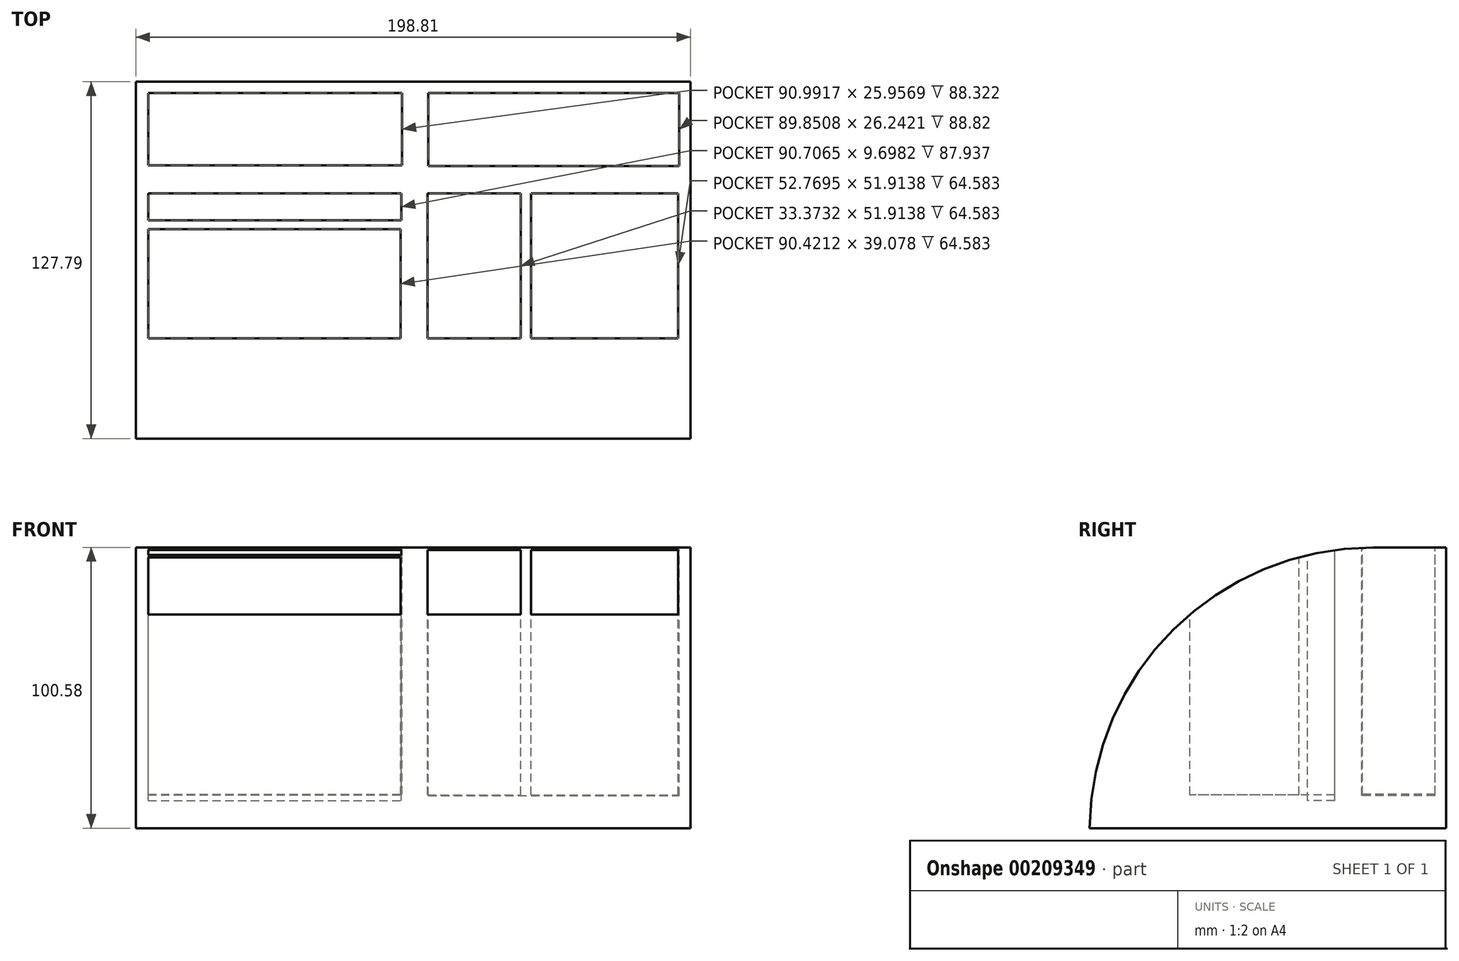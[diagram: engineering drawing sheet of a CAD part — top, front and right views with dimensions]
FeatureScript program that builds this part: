
annotation { "Feature Type Name" : "Feature", "Feature Type Description" : "" }
export const myFeature = defineFeature(function(context is Context, id is Id, definition is map)
    precondition{}
    {
        {
            var Q0;
            Q0=qCreatedBy(makeId("Top.planeOp"),FACE);
            var sketch = newSketch(context, id + "F0", { "sketchPlane" : qUnion([Q0])});
            skLineSegment(sketch, "E0.bottom", {"start": v(-100.12, 58.33) * mm, "end": v(98.7, 58.33) * mm});
            skLineSegment(sketch, "E0.top", {"start": v(-100.12, -69.46) * mm, "end": v(98.7, -69.46) * mm});
            skLineSegment(sketch, "E0.left", {"start": v(-100.12, 58.33) * mm, "end": v(-100.12, -69.46) * mm});
            skLineSegment(sketch, "E0.right", {"start": v(98.7, 58.33) * mm, "end": v(98.7, -69.46) * mm});
            skSolve(sketch);
        }
        {
            var Q0;
            Q0=makeQuery(id+"F0.imprint","IMPRINT",FACE,{"disambiguationData":[TD([[makeQuery(id+"F0.imprint","IMPRINT",EDGE,{"derivedFrom":sQuery(id+"F0.wireOp",EDGE,"E0.bottom")}),-1.0]])]});
            extrude(context, id + "F1", {"entities" : qUnion([Q0]), "oppositeDirection" : true, "depth" : 100.58 * mm});
        }
        {
            var Q0;
            Q0=makeQuery(id+"F1.opExtrude","CAP_EDGE",EDGE,{"disambiguationData":[OSD([sQuery(id+"F0.wireOp",EDGE,"E0.top")])],"isStart":true});
            fillet(context, id + "F2", {"entities" : qUnion([Q0]), "radius" : 101.6 * mm, "tangentPropagation" : true, "allowEdgeOverflow" : false});
        }
        {
            var Q0;
            Q0=qCreatedBy(makeId("Top.planeOp"),FACE);
            var sketch = newSketch(context, id + "F3", { "sketchPlane" : qUnion([Q0])});
            skLineSegment(sketch, "E1.bottom", {"start": v(-95.7, 54.34) * mm, "end": v(-4.7, 54.34) * mm});
            skLineSegment(sketch, "E1.top", {"start": v(-95.7, 28.38) * mm, "end": v(-4.7, 28.38) * mm});
            skLineSegment(sketch, "E1.left", {"start": v(-95.7, 54.34) * mm, "end": v(-95.7, 28.38) * mm});
            skLineSegment(sketch, "E1.right", {"start": v(-4.7, 54.34) * mm, "end": v(-4.7, 28.38) * mm});
            skSolve(sketch);
        }
        {
            var Q0;
            Q0=makeQuery(id+"F3.imprint","IMPRINT",FACE,{"disambiguationData":[TD([[makeQuery(id+"F3.imprint","IMPRINT",EDGE,{"derivedFrom":sQuery(id+"F3.wireOp",EDGE,"E1.bottom")}),-1.0]])]});
            extrude(context, id + "F4", {"entities" : qUnion([Q0]), "operationType" : NewBodyOperationType.REMOVE, "oppositeDirection" : true, "depth" : 88.4 * mm});
        }
        {
            var Q0;
            Q0=qCreatedBy(makeId("Top.planeOp"),FACE);
            var sketch = newSketch(context, id + "F5", { "sketchPlane" : qUnion([Q0])});
            skLineSegment(sketch, "E2.bottom", {"start": v(4.7, 54.34) * mm, "end": v(94.56, 54.34) * mm});
            skLineSegment(sketch, "E2.top", {"start": v(4.7, 28.1) * mm, "end": v(94.56, 28.1) * mm});
            skLineSegment(sketch, "E2.left", {"start": v(4.7, 54.34) * mm, "end": v(4.7, 28.1) * mm});
            skLineSegment(sketch, "E2.right", {"start": v(94.56, 54.34) * mm, "end": v(94.56, 28.1) * mm});
            skSolve(sketch);
        }
        {
            var Q0;
            Q0=makeQuery(id+"F5.imprint","IMPRINT",FACE,{"disambiguationData":[TD([[makeQuery(id+"F5.imprint","IMPRINT",EDGE,{"derivedFrom":sQuery(id+"F5.wireOp",EDGE,"E2.bottom")}),-1.0]])]});
            extrude(context, id + "F6", {"entities" : qUnion([Q0]), "operationType" : NewBodyOperationType.REMOVE, "oppositeDirection" : true, "depth" : 88.65 * mm});
        }
        {
            var Q0;
            Q0=makeQuery(id+"F4.boolean.opBoolean","COPY",FACE,{"derivedFrom":makeQuery(id+"F4.opExtrude","CAP_FACE",FACE,{"disambiguationData":[OSD([sQuery(id+"F3.wireOp",EDGE,"E1.bottom"),sQuery(id+"F3.wireOp",EDGE,"E1.top"),sQuery(id+"F3.wireOp",EDGE,"E1.left"),sQuery(id+"F3.wireOp",EDGE,"E1.right")])],"isStart":false})});
            extrude(context, id + "F7", {"entities" : qUnion([Q0]), "operationType" : NewBodyOperationType.REMOVE, "depth" : 0.25 * mm});
        }
        {
            var Q0;
            Q0=makeQuery(id+"F6.boolean.opBoolean","COPY",FACE,{"derivedFrom":makeQuery(id+"F6.opExtrude","CAP_FACE",FACE,{"disambiguationData":[OSD([sQuery(id+"F5.wireOp",EDGE,"E2.bottom"),sQuery(id+"F5.wireOp",EDGE,"E2.top"),sQuery(id+"F5.wireOp",EDGE,"E2.left"),sQuery(id+"F5.wireOp",EDGE,"E2.right")])],"isStart":false})});
            extrude(context, id + "F8", {"entities" : qUnion([Q0]), "operationType" : NewBodyOperationType.REMOVE, "oppositeDirection" : true, "depth" : 0.25 * mm});
        }
        {
            var Q0;
            Q0=qCreatedBy(makeId("Top.planeOp"),FACE);
            var sketch = newSketch(context, id + "F9", { "sketchPlane" : qUnion([Q0])});
            skLineSegment(sketch, "E3.bottom", {"start": v(-95.7, 18.4) * mm, "end": v(-5, 18.4) * mm});
            skLineSegment(sketch, "E3.top", {"start": v(-95.7, 8.7) * mm, "end": v(-5, 8.7) * mm});
            skLineSegment(sketch, "E3.left", {"start": v(-95.7, 18.4) * mm, "end": v(-95.7, 8.7) * mm});
            skLineSegment(sketch, "E3.right", {"start": v(-5, 18.4) * mm, "end": v(-5, 8.7) * mm});
            skSolve(sketch);
        }
        {
            var Q0;
            Q0=makeQuery(id+"F9.imprint","IMPRINT",FACE,{"disambiguationData":[TD([[makeQuery(id+"F9.imprint","IMPRINT",EDGE,{"derivedFrom":sQuery(id+"F9.wireOp",EDGE,"E3.bottom")}),-1.0]])]});
            extrude(context, id + "F10", {"entities" : qUnion([Q0]), "operationType" : NewBodyOperationType.REMOVE, "oppositeDirection" : true, "depth" : 90.68 * mm});
        }
        {
            var Q0;
            Q0=qCreatedBy(makeId("Top.planeOp"),FACE);
            var sketch = newSketch(context, id + "F11", { "sketchPlane" : qUnion([Q0])});
            skLineSegment(sketch, "E4.bottom", {"start": v(-95.7, 5.56) * mm, "end": v(-5.28, 5.56) * mm});
            skLineSegment(sketch, "E4.top", {"start": v(-95.7, -33.52) * mm, "end": v(-5.28, -33.52) * mm});
            skLineSegment(sketch, "E4.left", {"start": v(-95.7, 5.56) * mm, "end": v(-95.7, -33.52) * mm});
            skLineSegment(sketch, "E4.right", {"start": v(-5.28, 5.56) * mm, "end": v(-5.28, -33.52) * mm});
            skLineSegment(sketch, "E5.bottom", {"start": v(4.42, 18.4) * mm, "end": v(37.8, 18.4) * mm});
            skLineSegment(sketch, "E5.top", {"start": v(4.42, -33.52) * mm, "end": v(37.8, -33.52) * mm});
            skLineSegment(sketch, "E5.left", {"start": v(4.42, 18.4) * mm, "end": v(4.42, -33.52) * mm});
            skLineSegment(sketch, "E5.right", {"start": v(37.8, 18.4) * mm, "end": v(37.8, -33.52) * mm});
            skLineSegment(sketch, "E6.bottom", {"start": v(41.5, 18.4) * mm, "end": v(94.27, 18.4) * mm});
            skLineSegment(sketch, "E6.top", {"start": v(41.5, -33.52) * mm, "end": v(94.27, -33.52) * mm});
            skLineSegment(sketch, "E6.left", {"start": v(41.5, 18.4) * mm, "end": v(41.5, -33.52) * mm});
            skLineSegment(sketch, "E6.right", {"start": v(94.27, 18.4) * mm, "end": v(94.27, -33.52) * mm});
            skSolve(sketch);
        }
        {
            var Q0;
            Q0=makeQuery(id+"F11.imprint","IMPRINT",FACE,{"disambiguationData":[TD([[makeQuery(id+"F11.imprint","IMPRINT",EDGE,{"derivedFrom":sQuery(id+"F11.wireOp",EDGE,"E4.bottom")}),-1.0]])]});
            var Q1;
            Q1=makeQuery(id+"F11.imprint","IMPRINT",FACE,{"disambiguationData":[TD([[makeQuery(id+"F11.imprint","IMPRINT",EDGE,{"derivedFrom":sQuery(id+"F11.wireOp",EDGE,"E5.bottom")}),-1.0]])]});
            var Q2;
            Q2=makeQuery(id+"F11.imprint","IMPRINT",FACE,{"disambiguationData":[TD([[makeQuery(id+"F11.imprint","IMPRINT",EDGE,{"derivedFrom":sQuery(id+"F11.wireOp",EDGE,"E6.bottom")}),-1.0]])]});
            extrude(context, id + "F12", {"entities" : qUnion([Q0, Q1, Q2]), "operationType" : NewBodyOperationType.REMOVE, "oppositeDirection" : true, "depth" : 88.65 * mm});
        }
    });
